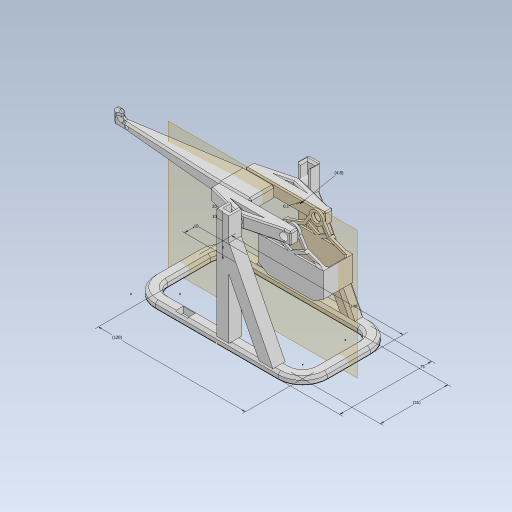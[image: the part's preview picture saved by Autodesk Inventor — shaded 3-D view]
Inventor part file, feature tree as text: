
AUTODESK INVENTOR PART (.ipt)
format: ipt  version: 2023 (Build 270158030, 158C)  size: 968,192 bytes
history: native  units: mm
features: sketch x23, extrude x20, chamfer x13, other x6, projected_geometry x6, mirror x5, plane x2, fillet x2
ambient origin geometry x8: Origin, YZ Plane, XZ Plane, XY Plane, X Axis, Y Axis, Z Axis, Center Point
bodies: Solid1 (feature_tree)
feature tree (77):
  sketch  "Sketch1"  dims[d0=75.0mm d1=140.0mm]
  extrude  "Extrusion1"  Depth=140.0mm
  extrude  "Extrusion2"  Depth=10.0mm
  sketch  "Sketch3"  dims[d4=20.0mm d5=5.0mm d6=0.0mm]
  extrude  "Extrusion5"  Depth=5.0mm TaperAngle=0.0deg
  extrude  "Extrusion6"  Depth=1.5mm
  extrude  "Extrusion3"  Depth=10.0mm
  extrude  "Extrusion7"  Depth=1.5mm
  extrude  "Extrusion9"  Depth=10.0mm
  extrude  "Extrusion10"  TaperAngle=0.0deg  [1 undecoded]
  extrude  "Extrusion11"  Depth=120.0mm
  plane  "Work Plane1"
  mirror  "Mirror1"
  other  "Work Point1"
  plane  "Work Plane2"
  extrude  "Extrusion12"  Depth=0.1mm
  extrude  "Extrusion13"  Depth=47.0mm
  extrude  "Extrusion14"  Depth=10.0mm
  extrude  "Extrusion15"  Depth=35.9mm
  extrude  "Extrusion17"  Depth=5.0mm
  extrude  "Extrusion18"  Depth=10.0mm
  chamfer  "Chamfer1"  Distance=90.0mm
  chamfer  "Chamfer2"  Distance=10.0mm
  chamfer  "Chamfer3"  Distance=5.0mm
  chamfer  "Chamfer4"  Distance=5.0mm
  extrude  "Extrusion19"  Depth=2.0mm
  chamfer  "Chamfer5"  Distance=11.205444mm
  chamfer  "Chamfer6"  [1 undecoded]
  fillet  "Fillet1"  Radius=6.2mm
  chamfer  "Chamfer7"  Distance=1.9mm
  chamfer  "Chamfer8"  Distance=1.9mm
  chamfer  "Chamfer9"  Distance=12.0mm
  fillet  "Fillet2"  Radius=6.2mm
  chamfer  "Chamfer10"  Distance=7.0mm
  chamfer  "Chamfer11"  Distance=6.0mm
  chamfer  "Chamfer12"  Distance=3.2mm
  mirror  "Mirror2"
  extrude  "Extrusion20"  Depth=10.0mm TaperAngle=0.0deg
  mirror  "Mirror3"
  extrude  "Extrusion21"  Depth=2.0mm
  extrude  "Extrusion22"  Depth=2.0mm
  mirror  "Mirror4"
  chamfer  "Chamfer13"  Distance=35.0mm
  extrude  "Extrusion23"  Depth=2.0mm
  mirror  "Mirror5"
  sketch  "Sketch28"  dims[d50=10.0mm d51=90.0mm d52=0.0mm d53=10.0mm d54=0.0mm d60=5.0mm d61=5.0mm d62=11.0mm d63=11.205444mm d64=0.0mm d65=0.0mm d66=6.2mm d67=1.9mm d68=1.9mm d69=12.0mm d70=6.2mm d71=7.0mm d72=0.0mm d73=6.0mm d74=3.2mm d75=10.0mm d76=0.0mm d77=7.0mm d78=30.0mm d79=35.0mm d80=7.0mm d82=7.0mm d83=7.0mm d84=21.0mm d85=2.0mm d86=8.0mm d87=0.0mm d88=0.0mm d89=6.0mm d90=5.0mm d91=5.0mm d92=0.0mm d93=0.0mm d94=5.0mm d95=5.0mm d96=21.0mm d98=0.0mm d99=5.0mm d100=10.0mm d101=8.0mm d102=8.0mm d103=120.0mm d104=10.0mm d105=5.0mm d106=0.0mm d107=0.0mm d108=5.0mm d109=12.0mm d110=0.0mm d111=0.0mm d119=6.0mm d120=5.0mm d121=10.0mm d122=0.0mm d123=7.0mm d124=6.0mm d125=0.0mm d126=1.0mm d127=2.0mm d128=45.0deg d129=1.0mm d130=2.0mm d131=45.0deg d132=1.0mm d133=2.0mm d134=45.0deg d135=1.0mm d136=2.0mm d137=45.0deg d138=2.5mm d139=2.8mm d140=12.0mm d141=0.0mm d142=0.0mm d143=25.0mm d144=6.0mm d145=2.0mm d146=2.0mm d147=45.0deg d148=2.0mm d149=2.0mm d150=45.0deg d151=2.0mm d152=2.0mm d153=2.0mm d154=45.0deg d155=1.0mm d156=2.0mm d157=45.0deg d158=1.5mm d159=2.0mm d160=45.0deg d161=2.0mm d162=1.5mm d163=2.0mm d164=45.0deg d165=2.0mm d166=2.0mm d167=45.0deg d168=1.5mm d169=2.0mm d170=45.0deg d171=0.5mm d172=2.0mm d173=8.0mm d174=5.0mm d175=16.0mm d176=6.0mm d177=20.0mm d178=5.0mm d179=16.0mm d180=8.0mm d181=8.0mm d182=2.0mm d183=2.0mm d184=0.0mm d185=2.0mm d186=0.0mm d187=1.5mm d188=0.0mm d189=1.5mm d190=2.0mm d191=45.0deg d192=1.0mm d193=1.0mm d194=1.0mm d195=1.0mm d196=1.5mm d197=0.0mm d198=0.1mm d199=4.8mm]
  sketch  "Sketch6"  dims[d9=2.5mm d10=10.0mm]
  sketch  "Sketch2"  dims[d2=10.0mm d3=10.0mm]
  sketch  "Sketch4"  dims[d7=6.0mm d8=1.5mm]
  projected_geometry  "Projected Loop1"
  other  "A-frame"
  sketch  "Sketch7"  dims[d11=5.0mm d12=1.5mm]
  projected_geometry  "Projected Loop2"
  other  "upright"
  sketch  "Sketch9"  dims[d13=6.0mm d14=10.0mm]
  projected_geometry  "Projected Loop3"
  sketch  "Sketch10"  dims[d15=60.0mm d16=0.0mm d17=0.0mm]
  sketch  "Sketch12"  dims[d18=55.0mm d19=120.0mm]
  sketch  "Sketch13"  dims[d22=0.1mm d23=0.1mm]
  sketch  "Sketch14"  dims[d24=5.0mm d25=0.0mm d30=47.0mm]
  other  "pivot"
  sketch  "Sketch15"  dims[d31=15.0mm d32=10.0mm]
  sketch  "Sketch16"  dims[d33=54.5mm d34=35.9mm]
  sketch  "Sketch17"  dims[d35=55.9mm d36=5.0mm]
  other  "throw-arm-top"
  sketch  "Sketch18"  dims[d37=5.0mm d38=10.0mm]
  sketch  "Sketch20"  dims[d39=25.0mm]
  sketch  "Sketch21"  dims[d40=25.0mm]
  sketch  "Sketch22"  dims[d41=0.1mm]
  sketch  "Sketch24"  dims[d42=5.0mm d43=5.0mm d44=0.0mm d45=0.0mm]
  other  "counterweight"
  sketch  "Sketch25"  dims[d47=10.0mm]
  projected_geometry  "Projected Loop5"
  sketch  "Sketch26"  dims[d48=0.9mm]
  projected_geometry  "Projected Loop6"
  sketch  "Sketch27"  dims[d49=0.5mm]
  projected_geometry  "Projected Loop7"
note: 2 required parameter values undecoded (feature->parameter linkage not recoverable at this tier; creation-order binding heuristic only, values carry confidence <= 0.55)
